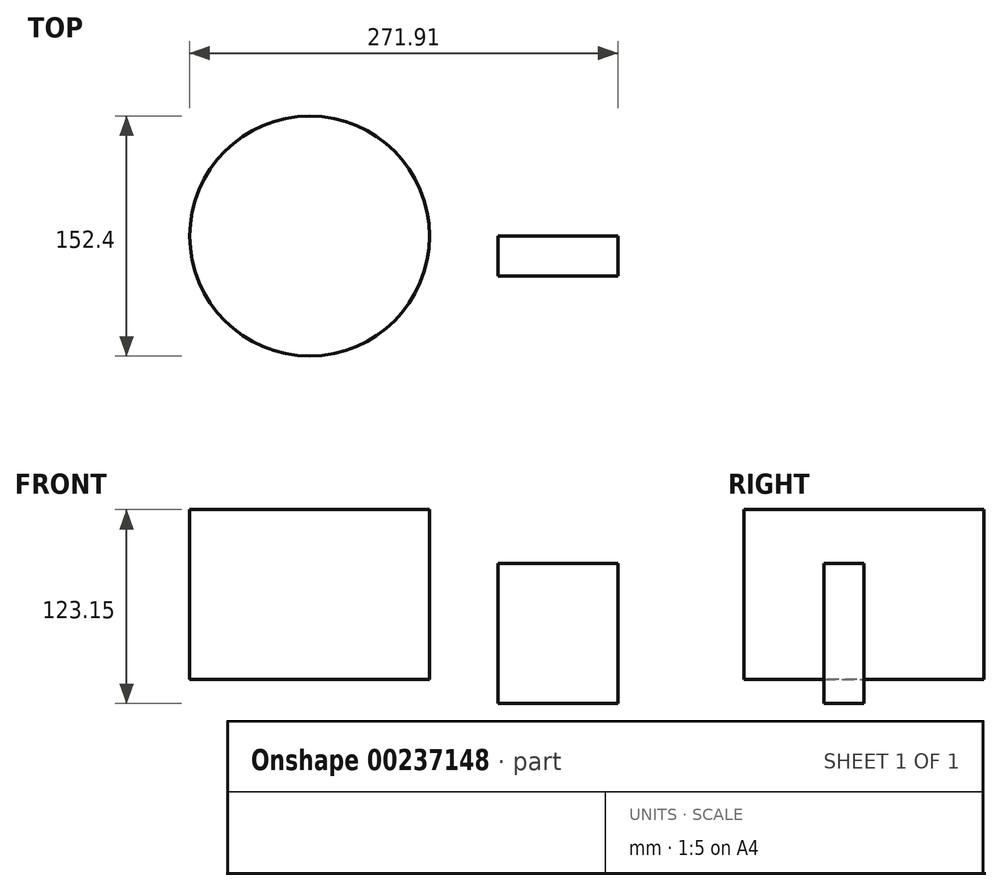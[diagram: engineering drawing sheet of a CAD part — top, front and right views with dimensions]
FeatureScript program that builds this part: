
annotation { "Feature Type Name" : "Feature", "Feature Type Description" : "" }
export const myFeature = defineFeature(function(context is Context, id is Id, definition is map)
    precondition{}
    {
        {
            var Q0;
            Q0=qCreatedBy(makeId("Top.planeOp"),FACE);
            var sketch = newSketch(context, id + "F0", { "sketchPlane" : qUnion([Q0])});
            skCircle(sketch, "E0", {"center": v(-23.34, 8.76) * mm, "radius": 38.52 * mm});
            skSolve(sketch);
        }
        {
            var Q0;
            Q0 = qSketchRegion(id + "F0", true);
            extrude(context, id + "F1", {"entities" : qUnion([Q0]), "depth" : 107.95 * mm});
        }
        {
            var Q0;
            Q0=makeQuery(id+"F1.opExtrude","SWEPT_BODY",BODY,{"disambiguationData":[OSD([sQuery(id+"F0.wireOp",EDGE,"E0")])]});
            deleteBodies(context, id + "F2", {"entities" : qUnion([Q0])});
        }
        {
            var Q0;
            Q0=qCreatedBy(makeId("Top.planeOp"),FACE);
            var sketch = newSketch(context, id + "F3", { "sketchPlane" : qUnion([Q0])});
            skCircle(sketch, "E1", {"center": v(-53.63, 0) * mm, "radius": 76.2 * mm});
            skSolve(sketch);
        }
        {
            var Q0;
            Q0 = qSketchRegion(id + "F3", true);
            extrude(context, id + "F4", {"entities" : qUnion([Q0]), "depth" : 107.95 * mm});
        }
        {
            var Q0;
            Q0=qCreatedBy(makeId("Front.planeOp"),FACE);
            var sketch = newSketch(context, id + "F5", { "sketchPlane" : qUnion([Q0])});
            skLineSegment(sketch, "E2.bottom", {"start": v(65.88, 73.7) * mm, "end": v(142.08, 73.7) * mm});
            skLineSegment(sketch, "E2.top", {"start": v(65.88, -15.2) * mm, "end": v(142.08, -15.2) * mm});
            skLineSegment(sketch, "E2.left", {"start": v(65.88, 73.7) * mm, "end": v(65.88, -15.2) * mm});
            skLineSegment(sketch, "E2.right", {"start": v(142.08, 73.7) * mm, "end": v(142.08, -15.2) * mm});
            skSolve(sketch);
        }
        {
            var Q0;
            Q0 = qSketchRegion(id + "F5", true);
            extrude(context, id + "F6", {"entities" : qUnion([Q0]), "depth" : 25.4 * mm});
        }
    });
